# Revit family: Crealco Palace OXX
name_source: partatom
category: Doors
revit_build: Autodesk Revit 2016 (Build: 20150714_1515(x64)
units: mm (PartAtom-declared; Revit-internal decimal feet)

## family parameters
Always vertical = Yes
Cut with Voids When Loaded = No
Host = Wall
OmniClass Number = 23.30.20.00
OmniClass Title = Windows
Room Calculation Point = No
Shared = No

## types (17) — shared parameters
Description = High Performance Sliding Door
Limit Glazing Thickness Max = 25 mm  [stored 0.082021 ft]
Limit Glazing Thickness Min = 6 mm  [stored 0.019685 ft]
Limit Sash Height Max = 2400 mm
Limit Sash Height Min = 300 mm  [stored 0.984252 ft]
Limit Sash Width Max = 1500 mm  [stored 4.92126 ft]
Limit Sash Width Min = 300 mm  [stored 0.984252 ft]
Limit Window Height Max = 2459 mm
Limit Window Height Min = 359 mm  [stored 1.17782 ft]
Limit Window Width Max = 4486 mm
Limit Window Width Min = 886 mm
Manufacturer = Crealco
Max Wind Load = 10000
Model = Palace
Sash Bottom Gap = 31 mm  [stored 0.101706 ft]
Sash Side Gap = 33 mm  [stored 0.108268 ft]
Sash Top Gap = 28 mm  [stored 0.0918635 ft]
Standard Interlock Ix = 25.866
URL = https://www.crealco.co.za
Wall Closure = By host
zero-valued in all types: Default Sill Height, Min Wind Load

## per-type parameters (varying)
| type | Standard Height | Standard Size | Standard Width | Type Comments |
| 2090 x 2090mm (Palace-2121OXX) | 2090 mm  [stored 6.85696 ft] | Yes | 2090 mm  [stored 6.85696 ft] | Palace-2121OXX |
| User Defined | 2090 mm  [stored 6.85696 ft] | No | 2090 mm  [stored 6.85696 ft] | Custom |
| 2390 x 2390mm (Palace-2424OXX) | 2390 mm  [stored 7.84121 ft] | Yes | 2390 mm  [stored 7.84121 ft] | Palace-2424OXX |
| 2690 x 2090mm (Palace-2721OXX) | 2090 mm  [stored 6.85696 ft] | Yes | 2690 mm | Palace-2721OXX |
| 2990 x 2090mm (Palace-3021OXX) | 2090 mm  [stored 6.85696 ft] | Yes | 2990 mm | Palace-3021OXX |
| 3290 x 2090mm (Palace-3321OXX) | 2090 mm  [stored 6.85696 ft] | Yes | 3290 mm | Palace-3321OXX |
| 3590 x 2090mm (Palace-3621OXX) | 2090 mm  [stored 6.85696 ft] | Yes | 3590 mm | Palace-3621OXX |
| 3890 x 2090mm (Palace-3921OXX) | 2090 mm  [stored 6.85696 ft] | Yes | 3890 mm  [stored 12.7625 ft] | Palace-3921OXX |
| 4190 x 2090mm (Palace-4221OXX) | 2090 mm  [stored 6.85696 ft] | Yes | 4190 mm  [stored 13.7467 ft] | Palace-4221OXX |
| 2090 x 2390mm (Palace-2124OXX) | 2390 mm  [stored 7.84121 ft] | Yes | 2090 mm  [stored 6.85696 ft] | Palace-2124OXX |
| 2390 x 2090mm (Palace-2421OXX) | 2090 mm  [stored 6.85696 ft] | Yes | 2390 mm  [stored 7.84121 ft] | Palace-2421OXX |
| 2690 x 2390mm (Palace-2724OXX) | 2390 mm  [stored 7.84121 ft] | Yes | 2690 mm | Palace-2724OXX |
| 2990 x 2390mm (Palace-3024OXX) | 2390 mm  [stored 7.84121 ft] | Yes | 2990 mm | Palace-3024OXX |
| 3290 x 2390mm (Palace-3324OXX) | 2390 mm  [stored 7.84121 ft] | Yes | 3290 mm | Palace-3324OXX |
| 3590 x 2390mm (Palace-3624OXX) | 2390 mm  [stored 7.84121 ft] | Yes | 3590 mm | Palace-3624OXX |
| 3890 x 2390mm (Palace-3924OXX) | 2390 mm  [stored 7.84121 ft] | Yes | 3890 mm  [stored 12.7625 ft] | Palace-3924OXX |
| 4190 x 2390mm (Palace-4224OXX) | 2390 mm  [stored 7.84121 ft] | Yes | 4190 mm  [stored 13.7467 ft] | Palace-4224OXX |

note: [stored X ft] marks values corroborated as IEEE doubles in the binary element streams (Revit-internal decimal feet)

## geometry (parser evidence)
native form markers: Sweep x38
no freeform markers — native parametric forms only
